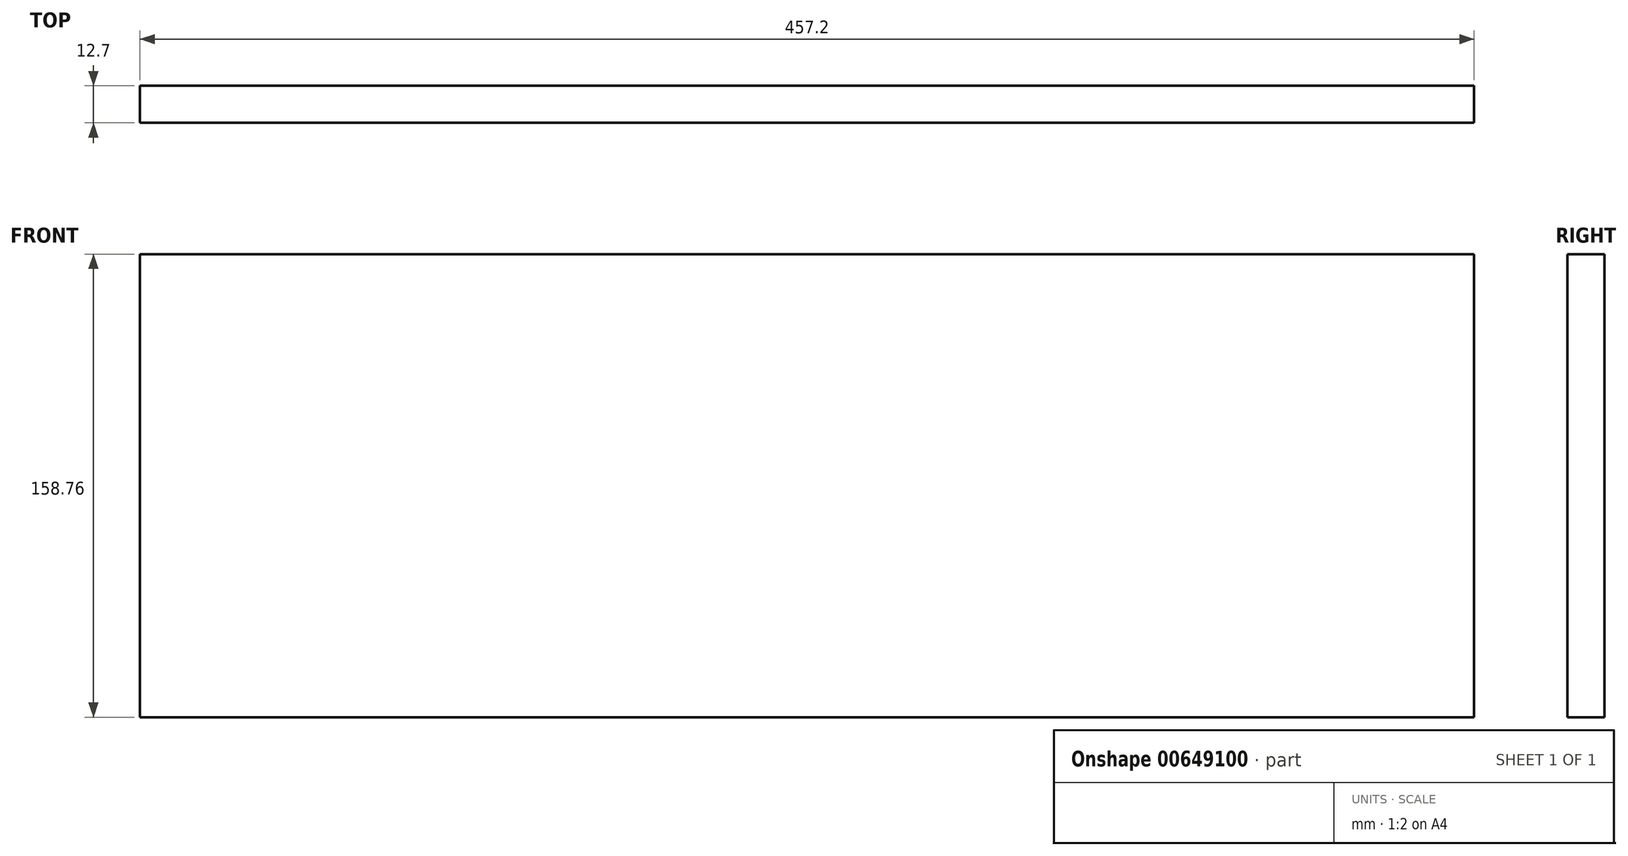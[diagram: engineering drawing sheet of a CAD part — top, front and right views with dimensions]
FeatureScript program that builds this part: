
annotation { "Feature Type Name" : "Feature", "Feature Type Description" : "" }
export const myFeature = defineFeature(function(context is Context, id is Id, definition is map)
    precondition{}
    {
        {
            var Q0;
            Q0=qCreatedBy(makeId("Front.planeOp"),FACE);
            var sketch = newSketch(context, id + "F0", { "sketchPlane" : qUnion([Q0])});
            skLineSegment(sketch, "E0.bottom", {"start": v(-228.6, 79.37) * mm, "end": v(228.6, 79.37) * mm});
            skLineSegment(sketch, "E0.top", {"start": v(-228.6, -79.37) * mm, "end": v(228.6, -79.37) * mm});
            skLineSegment(sketch, "E0.left", {"start": v(-228.6, 79.37) * mm, "end": v(-228.6, -79.37) * mm});
            skLineSegment(sketch, "E0.right", {"start": v(228.6, 79.37) * mm, "end": v(228.6, -79.37) * mm});
            skPoint(sketch, "E0.middle", {"position": v(0, 0) * mm});
            skSolve(sketch);
        }
        {
            var Q0;
            Q0=makeQuery(id+"F0.imprint","IMPRINT",FACE,{"disambiguationData":[TD([[makeQuery(id+"F0.imprint","IMPRINT",EDGE,{"derivedFrom":sQuery(id+"F0.wireOp",EDGE,"E0.bottom")}),-1.0]])]});
            extrude(context, id + "F1", {"entities" : qUnion([Q0]), "depth" : 12.7 * mm, "offsetDistance" : 25.4 * mm});
        }
    });
